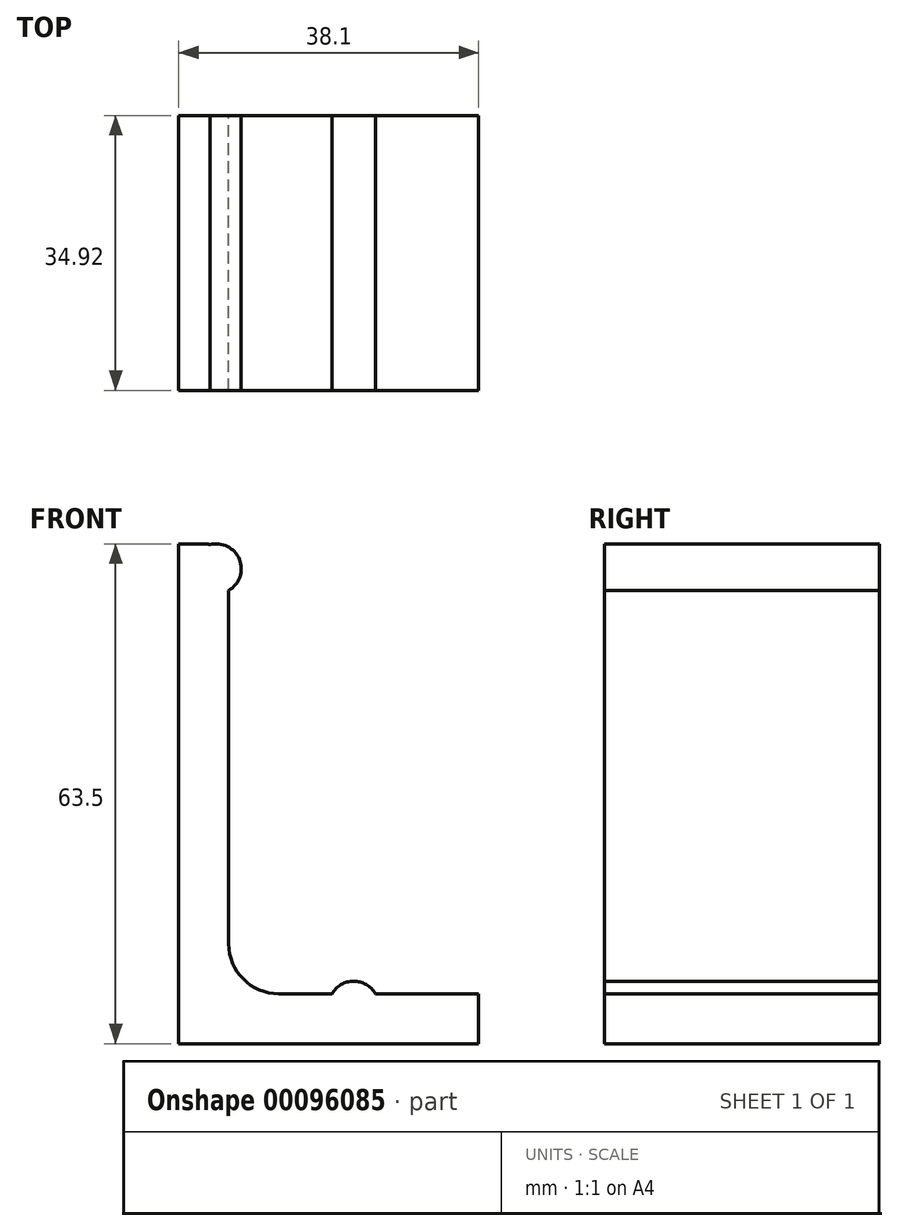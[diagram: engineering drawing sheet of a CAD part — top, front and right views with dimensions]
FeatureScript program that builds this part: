
annotation { "Feature Type Name" : "Feature", "Feature Type Description" : "" }
export const myFeature = defineFeature(function(context is Context, id is Id, definition is map)
    precondition{}
    {
        {
            var Q0;
            Q0=qCreatedBy(makeId("Front.planeOp"),FACE);
            var sketch = newSketch(context, id + "F0", { "sketchPlane" : qUnion([Q0])});
            skLineSegment(sketch, "E0", {"start": v(0, 63.5) * mm, "end": v(0, 0) * mm});
            skLineSegment(sketch, "E1", {"start": v(0, 0) * mm, "end": v(38.1, 0) * mm});
            skLineSegment(sketch, "E2", {"start": v(38.1, 0) * mm, "end": v(38.1, 6.35) * mm});
            skLineSegment(sketch, "E3", {"start": v(38.1, 6.35) * mm, "end": v(12.7, 6.35) * mm});
            skLineSegment(sketch, "E4", {"start": v(6.35, 12.7) * mm, "end": v(6.35, 60.33) * mm});
            skLineSegment(sketch, "E5", {"start": v(3.17, 63.5) * mm, "end": v(0, 63.5) * mm});
            skPoint(sketch, "E6.visualSharp", {"position": v(6.35, 6.35) * mm});
            skArc(sketch, "E6.filletArc", {"start": v(6.35, 12.7) * mm, "mid": v(8.2, 8.2) * mm, "end": v(12.7, 6.35) * mm});
            skPoint(sketch, "E7.visualSharp", {"position": v(6.35, 63.5) * mm});
            skArc(sketch, "E7.filletArc", {"start": v(6.35, 60.33) * mm, "mid": v(5.42, 62.57) * mm, "end": v(3.17, 63.5) * mm});
            skSolve(sketch);
        }
        {
            var Q0;
            Q0=makeQuery(id+"F0.imprint","IMPRINT",FACE,{"disambiguationData":[TD([[makeQuery(id+"F0.imprint","IMPRINT",EDGE,{"derivedFrom":sQuery(id+"F0.wireOp",EDGE,"E0")}),1.0]])]});
            extrude(context, id + "F1", {"entities" : qUnion([Q0]), "depth" : 34.92 * mm});
        }
        {
            var Q0;
            Q0=makeQuery(id+"F1.opExtrude","CAP_FACE",FACE,{"disambiguationData":[OSD([sQuery(id+"F0.wireOp",EDGE,"E0"),sQuery(id+"F0.wireOp",EDGE,"E1"),sQuery(id+"F0.wireOp",EDGE,"E2"),sQuery(id+"F0.wireOp",EDGE,"E3"),sQuery(id+"F0.wireOp",EDGE,"E4"),sQuery(id+"F0.wireOp",EDGE,"E5"),sQuery(id+"F0.wireOp",EDGE,"E6.filletArc"),sQuery(id+"F0.wireOp",EDGE,"E7.filletArc")])],"isStart":false});
            var sketch = newSketch(context, id + "F2", { "sketchPlane" : qUnion([Q0])});
            skCircle(sketch, "E8", {"center": v(4.76, 60.33) * mm, "radius": 3.18 * mm});
            skLineSegment(sketch, "E9", {"start": v(6.35, 60.33) * mm, "end": v(0, 60.33) * mm, "construction": true});
            skCircle(sketch, "E10", {"center": v(22.23, 4.76) * mm, "radius": 3.18 * mm});
            skSolve(sketch);
        }
        {
            var Q0;
            Q0 = qSketchRegion(id + "F2", true);
            var Q1;
            Q1=makeQuery(id+"F1.opExtrude","CAP_FACE",FACE,{"disambiguationData":[OSD([sQuery(id+"F0.wireOp",EDGE,"E0"),sQuery(id+"F0.wireOp",EDGE,"E1"),sQuery(id+"F0.wireOp",EDGE,"E2"),sQuery(id+"F0.wireOp",EDGE,"E3"),sQuery(id+"F0.wireOp",EDGE,"E4"),sQuery(id+"F0.wireOp",EDGE,"E5"),sQuery(id+"F0.wireOp",EDGE,"E6.filletArc"),sQuery(id+"F0.wireOp",EDGE,"E7.filletArc")])],"isStart":true});
            extrude(context, id + "F3", {"entities" : qUnion([Q0]), "operationType" : NewBodyOperationType.ADD, "endBound" : BoundingType.UP_TO_SURFACE, "oppositeDirection" : true, "endBoundEntityFace" : qUnion([Q1]), "depth" : 25.4 * mm});
        }
    });
